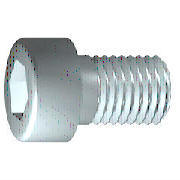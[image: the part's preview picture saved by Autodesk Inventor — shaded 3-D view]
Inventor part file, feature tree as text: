
AUTODESK INVENTOR PART (.ipt)
format: ipt  version: 2022 (Build 260153000, 153)  size: 193,536 bytes
history: native  units: mm (DEFAULTED — no unit token found)
features: sketch x2, other x1, extrude x1, plane x1, fillet x1
ambient origin geometry x7: Origin, YZ Plane, XY Plane, X Axis, Y Axis, Z Axis, Center Point
bodies: Solid1 (feature_tree)
feature tree (6):
  other  "Базовый элемент"
  extrude  "Паз"  Depth=8.75mm
  plane  "Work Plane1"
  fillet  "Fillet2"  Radius=0.306825mm
  sketch  "Эскиз1"
  sketch  "Эскиз2"
